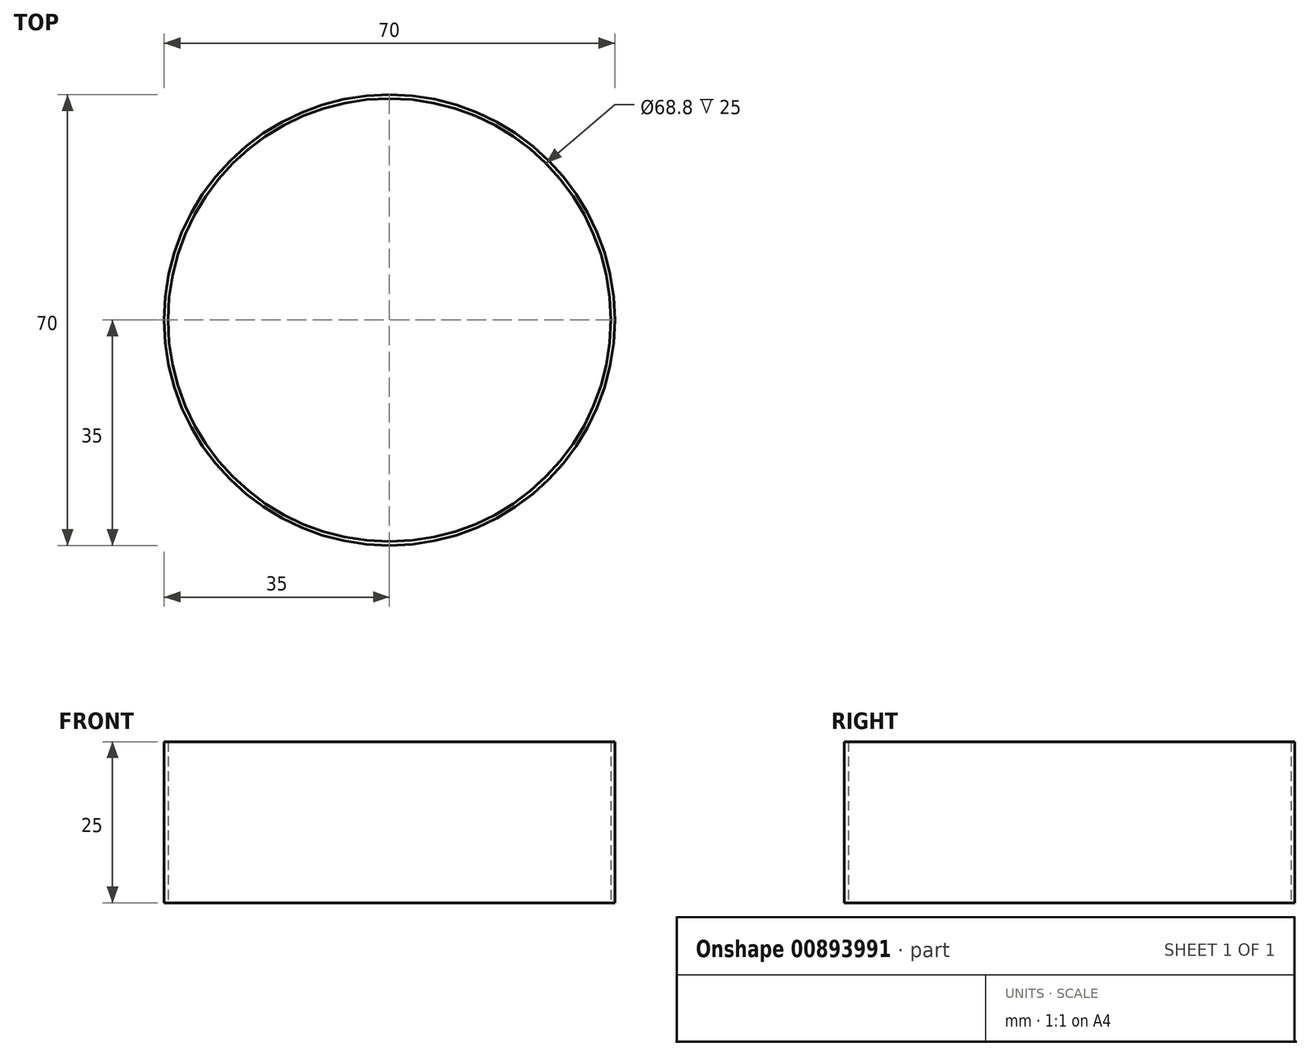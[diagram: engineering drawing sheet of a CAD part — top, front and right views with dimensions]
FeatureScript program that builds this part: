
annotation { "Feature Type Name" : "Feature", "Feature Type Description" : "" }
export const myFeature = defineFeature(function(context is Context, id is Id, definition is map)
    precondition{}
    {
        {
            var Q0;
            Q0=qCreatedBy(makeId("Top.planeOp"),FACE);
            var sketch = newSketch(context, id + "F0", { "sketchPlane" : qUnion([Q0])});
            skCircle(sketch, "E0", {"center": v(0, 0) * mm, "radius": 35 * mm});
            skCircle(sketch, "E1", {"center": v(0, 0) * mm, "radius": 34.4 * mm});
            skSolve(sketch);
        }
        {
            var Q0;
            Q0=makeQuery(id+"F0.imprint","IMPRINT",FACE,{"disambiguationData":[TD([[makeQuery(id+"F0.imprint","IMPRINT",EDGE,{"derivedFrom":sQuery(id+"F0.wireOp",EDGE,"E0")}),1.0]])]});
            extrude(context, id + "F1", {"entities" : qUnion([Q0]), "depth" : 25 * mm, "offsetDistance" : 25 * mm});
        }
    });
